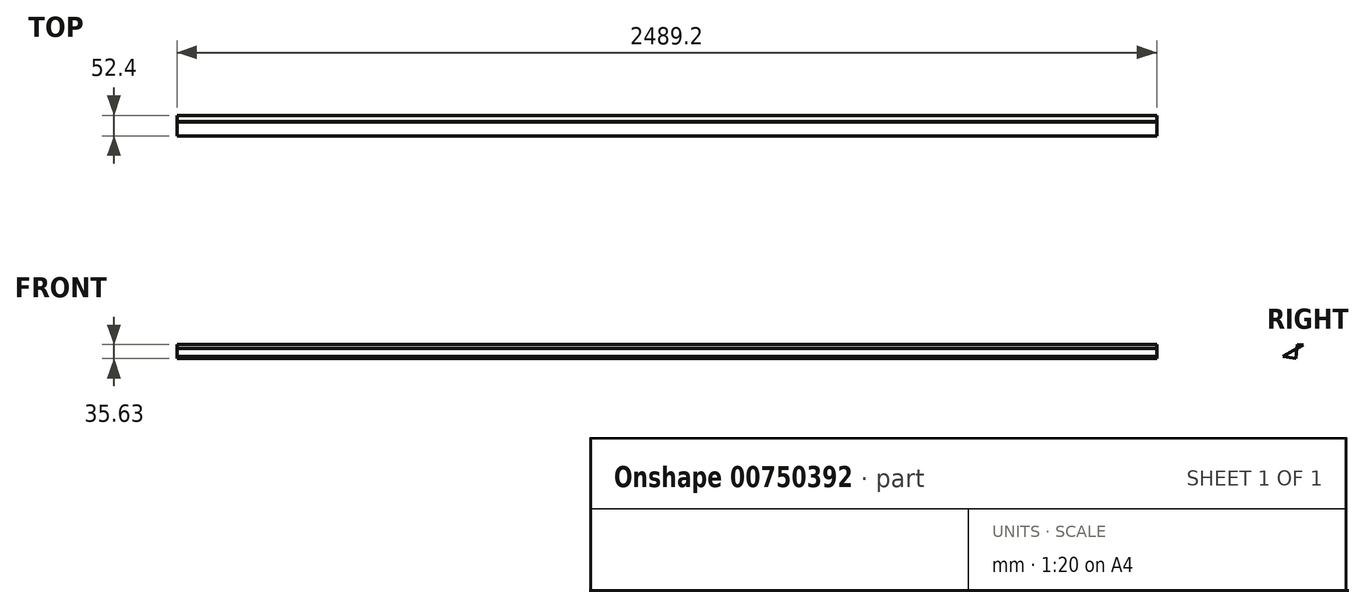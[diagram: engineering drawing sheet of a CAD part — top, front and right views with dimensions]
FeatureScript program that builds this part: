
annotation { "Feature Type Name" : "Feature", "Feature Type Description" : "" }
export const myFeature = defineFeature(function(context is Context, id is Id, definition is map)
    precondition{}
    {
        {
            var Q0;
            Q0=qCreatedBy(makeId("Right.planeOp"),FACE);
            var sketch = newSketch(context, id + "F0", { "sketchPlane" : qUnion([Q0])});
            skLineSegment(sketch, "E0", {"start": v(-473.2, -436.13) * mm, "end": v(-161.12, -207.43) * mm});
            skLineSegment(sketch, "E1", {"start": v(-473.2, -436.13) * mm, "end": v(-274.01, -449.43) * mm});
            skLineSegment(sketch, "E2", {"start": v(-473.2, -436.13) * mm, "end": v(-514.07, -862.73) * mm});
            skLineSegment(sketch, "E3", {"start": v(-510, -466.04) * mm, "end": v(-562.2, -708.47) * mm});
            skLineSegment(sketch, "E4", {"start": v(-510, -466.04) * mm, "end": v(-12.3, -191.8) * mm});
            skLineSegment(sketch, "E5", {"start": v(-510, -466.04) * mm, "end": v(-239.42, -512.4) * mm});
            skSolve(sketch);
        }
        {
            var Q0;
            Q0 = qSketchRegion(id + "F0", true);
            extrude(context, id + "F1", {"entities" : qUnion([Q0]), "depth" : 2489.2 * mm, "offsetDistance" : 25.4 * mm});
        }
    });
